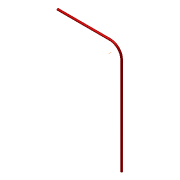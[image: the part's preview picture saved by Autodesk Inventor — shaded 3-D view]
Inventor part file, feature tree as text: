
AUTODESK INVENTOR PART (.ipt)
format: ipt  version: unknown  size: 166,400 bytes
history: native  units: in
note: dims shown in document units (in); Inventor stores cm internally (conversion verified against a paired STEP export)
features: sketch x2, sweep x1, other x1
ambient origin geometry x8: Origin, YZ Plane, XZ Plane, XY Plane, X Axis, Y Axis, Z Axis, Center Point
feature tree (4):
  sweep  "Sweep7"
  other  "Work Axis11"
  sketch  "Sketch21"  dims[d66=0.4724in d68=1.063in]
  sketch  "Sketch22"  dims[d69=0.0394in d70=0.0in d72=1.9685in]
